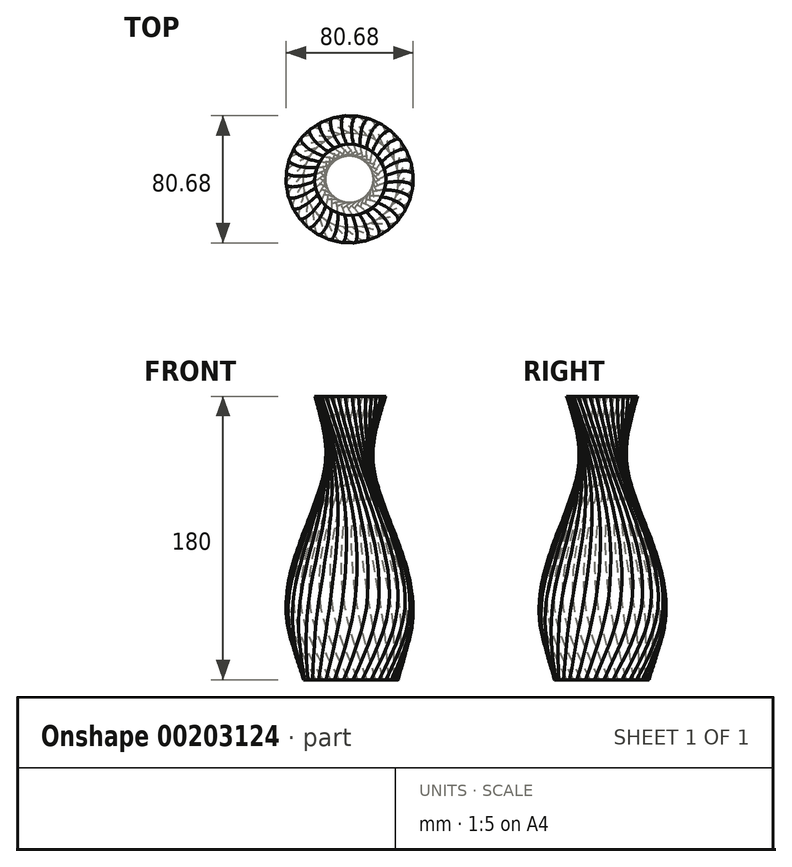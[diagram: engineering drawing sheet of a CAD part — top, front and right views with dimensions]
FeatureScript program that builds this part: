
annotation { "Feature Type Name" : "Feature", "Feature Type Description" : "" }
export const myFeature = defineFeature(function(context is Context, id is Id, definition is map)
    precondition{}
    {
        {
            var Q0;
            Q0=qCreatedBy(makeId("Top.planeOp"),FACE);
            var sketch = newSketch(context, id + "F0", { "sketchPlane" : qUnion([Q0])});
            skCircle(sketch, "E0.cCircle", {"center": v(0, 0) * mm, "radius": 30 * mm, "construction": true});
            skLineSegment(sketch, "E0.0", {"start": v(25.76, -15.66) * mm, "end": v(22.2, -20.39) * mm});
            skLineSegment(sketch, "E0.1", {"start": v(22.2, -20.39) * mm, "end": v(17.8, -24.33) * mm});
            skLineSegment(sketch, "E0.2", {"start": v(17.8, -24.33) * mm, "end": v(12.71, -27.33) * mm});
            skLineSegment(sketch, "E0.3", {"start": v(12.71, -27.33) * mm, "end": v(7.14, -29.29) * mm});
            skLineSegment(sketch, "E0.4", {"start": v(7.14, -29.29) * mm, "end": v(1.29, -30.12) * mm});
            skLineSegment(sketch, "E0.5", {"start": v(1.29, -30.12) * mm, "end": v(-4.61, -29.79) * mm});
            skLineSegment(sketch, "E0.6", {"start": v(-4.61, -29.79) * mm, "end": v(-10.34, -28.32) * mm});
            skLineSegment(sketch, "E0.7", {"start": v(-10.34, -28.32) * mm, "end": v(-15.66, -25.76) * mm});
            skLineSegment(sketch, "E0.8", {"start": v(-15.66, -25.76) * mm, "end": v(-20.39, -22.2) * mm});
            skLineSegment(sketch, "E0.9", {"start": v(-20.39, -22.2) * mm, "end": v(-24.33, -17.8) * mm});
            skLineSegment(sketch, "E0.10", {"start": v(-24.33, -17.8) * mm, "end": v(-27.33, -12.71) * mm});
            skLineSegment(sketch, "E0.11", {"start": v(-27.33, -12.71) * mm, "end": v(-29.29, -7.14) * mm});
            skLineSegment(sketch, "E0.12", {"start": v(-29.29, -7.14) * mm, "end": v(-30.12, -1.29) * mm});
            skLineSegment(sketch, "E0.13", {"start": v(-30.12, -1.29) * mm, "end": v(-29.79, 4.61) * mm});
            skLineSegment(sketch, "E0.14", {"start": v(-29.79, 4.61) * mm, "end": v(-28.32, 10.34) * mm});
            skLineSegment(sketch, "E0.15", {"start": v(-28.32, 10.34) * mm, "end": v(-25.76, 15.66) * mm});
            skLineSegment(sketch, "E0.16", {"start": v(-25.76, 15.66) * mm, "end": v(-22.2, 20.39) * mm});
            skLineSegment(sketch, "E0.17", {"start": v(-22.2, 20.39) * mm, "end": v(-17.8, 24.33) * mm});
            skLineSegment(sketch, "E0.18", {"start": v(-17.8, 24.33) * mm, "end": v(-12.71, 27.33) * mm});
            skLineSegment(sketch, "E0.19", {"start": v(-12.71, 27.33) * mm, "end": v(-7.14, 29.29) * mm});
            skLineSegment(sketch, "E0.20", {"start": v(-7.14, 29.29) * mm, "end": v(-1.29, 30.12) * mm});
            skLineSegment(sketch, "E0.21", {"start": v(-1.29, 30.12) * mm, "end": v(4.61, 29.79) * mm});
            skLineSegment(sketch, "E0.22", {"start": v(4.61, 29.79) * mm, "end": v(10.34, 28.32) * mm});
            skLineSegment(sketch, "E0.23", {"start": v(10.34, 28.32) * mm, "end": v(15.66, 25.76) * mm});
            skLineSegment(sketch, "E0.24", {"start": v(15.66, 25.76) * mm, "end": v(20.39, 22.2) * mm});
            skLineSegment(sketch, "E0.25", {"start": v(20.39, 22.2) * mm, "end": v(24.33, 17.8) * mm});
            skLineSegment(sketch, "E0.26", {"start": v(24.33, 17.8) * mm, "end": v(27.33, 12.71) * mm});
            skLineSegment(sketch, "E0.27", {"start": v(27.33, 12.71) * mm, "end": v(29.29, 7.14) * mm});
            skLineSegment(sketch, "E0.28", {"start": v(29.29, 7.14) * mm, "end": v(30.12, 1.29) * mm});
            skLineSegment(sketch, "E0.29", {"start": v(30.12, 1.29) * mm, "end": v(29.79, -4.61) * mm});
            skLineSegment(sketch, "E0.30", {"start": v(29.79, -4.61) * mm, "end": v(28.32, -10.34) * mm});
            skLineSegment(sketch, "E0.31", {"start": v(28.32, -10.34) * mm, "end": v(25.76, -15.66) * mm});
            skPoint(sketch, "E0.0.midPoint", {"position": v(23.98, -18.02) * mm});
            skSolve(sketch);
        }
        {
            var Q0;
            Q0=qCreatedBy(makeId("Top.planeOp"),FACE);
            cPlane(context, id + "F1", {"entities" : qUnion([Q0]), "cplaneType" : CPlaneType.OFFSET, "offset" : 40 * mm, "width" : 150 * mm, "height" : 150 * mm});
        }
        {
            var Q0;
            Q0=qCreatedBy(id+"F1.planeOp",FACE);
            var sketch = newSketch(context, id + "F2", { "sketchPlane" : qUnion([Q0])});
            skCircle(sketch, "E1.cCircle", {"center": v(-0.7, 0.53) * mm, "radius": 40 * mm, "construction": true});
            skLineSegment(sketch, "E1.0", {"start": v(33.64, -20.35) * mm, "end": v(28.9, -26.65) * mm});
            skLineSegment(sketch, "E1.1", {"start": v(28.9, -26.65) * mm, "end": v(23.03, -31.9) * mm});
            skLineSegment(sketch, "E1.2", {"start": v(23.03, -31.9) * mm, "end": v(16.25, -35.91) * mm});
            skLineSegment(sketch, "E1.3", {"start": v(16.25, -35.91) * mm, "end": v(8.81, -38.52) * mm});
            skLineSegment(sketch, "E1.4", {"start": v(8.81, -38.52) * mm, "end": v(1, -39.63) * mm});
            skLineSegment(sketch, "E1.5", {"start": v(1, -39.63) * mm, "end": v(-6.86, -39.19) * mm});
            skLineSegment(sketch, "E1.6", {"start": v(-6.86, -39.19) * mm, "end": v(-14.49, -37.23) * mm});
            skLineSegment(sketch, "E1.7", {"start": v(-14.49, -37.23) * mm, "end": v(-21.59, -33.81) * mm});
            skLineSegment(sketch, "E1.8", {"start": v(-21.59, -33.81) * mm, "end": v(-27.89, -29.08) * mm});
            skLineSegment(sketch, "E1.9", {"start": v(-27.89, -29.08) * mm, "end": v(-33.14, -23.2) * mm});
            skLineSegment(sketch, "E1.10", {"start": v(-33.14, -23.2) * mm, "end": v(-37.15, -16.42) * mm});
            skLineSegment(sketch, "E1.11", {"start": v(-37.15, -16.42) * mm, "end": v(-39.76, -8.99) * mm});
            skLineSegment(sketch, "E1.12", {"start": v(-39.76, -8.99) * mm, "end": v(-40.86, -1.18) * mm});
            skLineSegment(sketch, "E1.13", {"start": v(-40.86, -1.18) * mm, "end": v(-40.43, 6.68) * mm});
            skLineSegment(sketch, "E1.14", {"start": v(-40.43, 6.68) * mm, "end": v(-38.46, 14.31) * mm});
            skLineSegment(sketch, "E1.15", {"start": v(-38.46, 14.31) * mm, "end": v(-35.05, 21.41) * mm});
            skLineSegment(sketch, "E1.16", {"start": v(-35.05, 21.41) * mm, "end": v(-30.31, 27.71) * mm});
            skLineSegment(sketch, "E1.17", {"start": v(-30.31, 27.71) * mm, "end": v(-24.44, 32.97) * mm});
            skLineSegment(sketch, "E1.18", {"start": v(-24.44, 32.97) * mm, "end": v(-17.66, 36.97) * mm});
            skLineSegment(sketch, "E1.19", {"start": v(-17.66, 36.97) * mm, "end": v(-10.22, 39.58) * mm});
            skLineSegment(sketch, "E1.20", {"start": v(-10.22, 39.58) * mm, "end": v(-2.42, 40.69) * mm});
            skLineSegment(sketch, "E1.21", {"start": v(-2.42, 40.69) * mm, "end": v(5.45, 40.25) * mm});
            skLineSegment(sketch, "E1.22", {"start": v(5.45, 40.25) * mm, "end": v(13.08, 38.29) * mm});
            skLineSegment(sketch, "E1.23", {"start": v(13.08, 38.29) * mm, "end": v(20.18, 34.87) * mm});
            skLineSegment(sketch, "E1.24", {"start": v(20.18, 34.87) * mm, "end": v(26.48, 30.14) * mm});
            skLineSegment(sketch, "E1.25", {"start": v(26.48, 30.14) * mm, "end": v(31.73, 24.27) * mm});
            skLineSegment(sketch, "E1.26", {"start": v(31.73, 24.27) * mm, "end": v(35.74, 17.48) * mm});
            skLineSegment(sketch, "E1.27", {"start": v(35.74, 17.48) * mm, "end": v(38.35, 10.05) * mm});
            skLineSegment(sketch, "E1.28", {"start": v(38.35, 10.05) * mm, "end": v(39.45, 2.25) * mm});
            skLineSegment(sketch, "E1.29", {"start": v(39.45, 2.25) * mm, "end": v(39.01, -5.62) * mm});
            skLineSegment(sketch, "E1.30", {"start": v(39.01, -5.62) * mm, "end": v(37.05, -13.25) * mm});
            skLineSegment(sketch, "E1.31", {"start": v(37.05, -13.25) * mm, "end": v(33.64, -20.35) * mm});
            skPoint(sketch, "E1.0.midPoint", {"position": v(31.27, -23.5) * mm});
            skSolve(sketch);
        }
        {
            var Q0;
            Q0=qCreatedBy(id+"F1.planeOp",FACE);
            cPlane(context, id + "F3", {"entities" : qUnion([Q0]), "cplaneType" : CPlaneType.OFFSET, "offset" : 100 * mm, "width" : 150 * mm, "height" : 150 * mm});
        }
        {
            var Q0;
            Q0=qCreatedBy(id+"F3.planeOp",FACE);
            var sketch = newSketch(context, id + "F4", { "sketchPlane" : qUnion([Q0])});
            skCircle(sketch, "E2.cCircle", {"center": v(-0.94, 0.7) * mm, "radius": 15 * mm, "construction": true});
            skLineSegment(sketch, "E2.0", {"start": v(11.94, -7.12) * mm, "end": v(10.16, -9.49) * mm});
            skLineSegment(sketch, "E2.1", {"start": v(10.16, -9.49) * mm, "end": v(7.96, -11.46) * mm});
            skLineSegment(sketch, "E2.2", {"start": v(7.96, -11.46) * mm, "end": v(5.42, -12.96) * mm});
            skLineSegment(sketch, "E2.3", {"start": v(5.42, -12.96) * mm, "end": v(2.63, -13.94) * mm});
            skLineSegment(sketch, "E2.4", {"start": v(2.63, -13.94) * mm, "end": v(-0.3, -14.35) * mm});
            skLineSegment(sketch, "E2.5", {"start": v(-0.3, -14.35) * mm, "end": v(-3.25, -14.19) * mm});
            skLineSegment(sketch, "E2.6", {"start": v(-3.25, -14.19) * mm, "end": v(-6.1, -13.45) * mm});
            skLineSegment(sketch, "E2.7", {"start": v(-6.1, -13.45) * mm, "end": v(-8.77, -12.17) * mm});
            skLineSegment(sketch, "E2.8", {"start": v(-8.77, -12.17) * mm, "end": v(-11.13, -10.4) * mm});
            skLineSegment(sketch, "E2.9", {"start": v(-11.13, -10.4) * mm, "end": v(-13.1, -8.2) * mm});
            skLineSegment(sketch, "E2.10", {"start": v(-13.1, -8.2) * mm, "end": v(-14.6, -5.65) * mm});
            skLineSegment(sketch, "E2.11", {"start": v(-14.6, -5.65) * mm, "end": v(-15.58, -2.86) * mm});
            skLineSegment(sketch, "E2.12", {"start": v(-15.58, -2.86) * mm, "end": v(-16, 0.06) * mm});
            skLineSegment(sketch, "E2.13", {"start": v(-16, 0.06) * mm, "end": v(-15.84, 3.01) * mm});
            skLineSegment(sketch, "E2.14", {"start": v(-15.84, 3.01) * mm, "end": v(-15.1, 5.88) * mm});
            skLineSegment(sketch, "E2.15", {"start": v(-15.1, 5.88) * mm, "end": v(-13.82, 8.54) * mm});
            skLineSegment(sketch, "E2.16", {"start": v(-13.82, 8.54) * mm, "end": v(-12.04, 10.9) * mm});
            skLineSegment(sketch, "E2.17", {"start": v(-12.04, 10.9) * mm, "end": v(-9.84, 12.87) * mm});
            skLineSegment(sketch, "E2.18", {"start": v(-9.84, 12.87) * mm, "end": v(-7.3, 14.37) * mm});
            skLineSegment(sketch, "E2.19", {"start": v(-7.3, 14.37) * mm, "end": v(-4.5, 15.35) * mm});
            skLineSegment(sketch, "E2.20", {"start": v(-4.5, 15.35) * mm, "end": v(-1.58, 15.77) * mm});
            skLineSegment(sketch, "E2.21", {"start": v(-1.58, 15.77) * mm, "end": v(1.37, 15.6) * mm});
            skLineSegment(sketch, "E2.22", {"start": v(1.37, 15.6) * mm, "end": v(4.23, 14.87) * mm});
            skLineSegment(sketch, "E2.23", {"start": v(4.23, 14.87) * mm, "end": v(6.9, 13.59) * mm});
            skLineSegment(sketch, "E2.24", {"start": v(6.9, 13.59) * mm, "end": v(9.25, 11.8) * mm});
            skLineSegment(sketch, "E2.25", {"start": v(9.25, 11.8) * mm, "end": v(11.22, 9.6) * mm});
            skLineSegment(sketch, "E2.26", {"start": v(11.22, 9.6) * mm, "end": v(12.73, 7.06) * mm});
            skLineSegment(sketch, "E2.27", {"start": v(12.73, 7.06) * mm, "end": v(13.7, 4.28) * mm});
            skLineSegment(sketch, "E2.28", {"start": v(13.7, 4.28) * mm, "end": v(14.12, 1.35) * mm});
            skLineSegment(sketch, "E2.29", {"start": v(14.12, 1.35) * mm, "end": v(13.95, -1.6) * mm});
            skLineSegment(sketch, "E2.30", {"start": v(13.95, -1.6) * mm, "end": v(13.22, -4.46) * mm});
            skLineSegment(sketch, "E2.31", {"start": v(13.22, -4.46) * mm, "end": v(11.94, -7.12) * mm});
            skPoint(sketch, "E2.0.midPoint", {"position": v(11.05, -8.3) * mm});
            skSolve(sketch);
        }
        {
            var Q0;
            Q0=qCreatedBy(id+"F3.planeOp",FACE);
            cPlane(context, id + "F5", {"entities" : qUnion([Q0]), "cplaneType" : CPlaneType.OFFSET, "offset" : 40 * mm, "width" : 150 * mm, "height" : 150 * mm});
        }
        {
            var Q0;
            Q0=qCreatedBy(id+"F5.planeOp",FACE);
            var sketch = newSketch(context, id + "F6", { "sketchPlane" : qUnion([Q0])});
            skCircle(sketch, "E3.cCircle", {"center": v(-0.35, 0.27) * mm, "radius": 22.5 * mm, "construction": true});
            skLineSegment(sketch, "E3.0", {"start": v(18.96, -11.48) * mm, "end": v(16.3, -15.03) * mm});
            skLineSegment(sketch, "E3.1", {"start": v(16.3, -15.03) * mm, "end": v(13, -17.98) * mm});
            skLineSegment(sketch, "E3.2", {"start": v(13, -17.98) * mm, "end": v(9.18, -20.23) * mm});
            skLineSegment(sketch, "E3.3", {"start": v(9.18, -20.23) * mm, "end": v(5, -21.7) * mm});
            skLineSegment(sketch, "E3.4", {"start": v(5, -21.7) * mm, "end": v(0.61, -22.32) * mm});
            skLineSegment(sketch, "E3.5", {"start": v(0.61, -22.32) * mm, "end": v(-3.81, -22.08) * mm});
            skLineSegment(sketch, "E3.6", {"start": v(-3.81, -22.08) * mm, "end": v(-8.1, -20.97) * mm});
            skLineSegment(sketch, "E3.7", {"start": v(-8.1, -20.97) * mm, "end": v(-12.1, -19.05) * mm});
            skLineSegment(sketch, "E3.8", {"start": v(-12.1, -19.05) * mm, "end": v(-15.64, -16.39) * mm});
            skLineSegment(sketch, "E3.9", {"start": v(-15.64, -16.39) * mm, "end": v(-18.6, -13.09) * mm});
            skLineSegment(sketch, "E3.10", {"start": v(-18.6, -13.09) * mm, "end": v(-20.85, -9.27) * mm});
            skLineSegment(sketch, "E3.11", {"start": v(-20.85, -9.27) * mm, "end": v(-22.32, -5.09) * mm});
            skLineSegment(sketch, "E3.12", {"start": v(-22.32, -5.09) * mm, "end": v(-22.94, -0.7) * mm});
            skLineSegment(sketch, "E3.13", {"start": v(-22.94, -0.7) * mm, "end": v(-22.7, 3.73) * mm});
            skLineSegment(sketch, "E3.14", {"start": v(-22.7, 3.73) * mm, "end": v(-21.6, 8.02) * mm});
            skLineSegment(sketch, "E3.15", {"start": v(-21.6, 8.02) * mm, "end": v(-19.67, 12.01) * mm});
            skLineSegment(sketch, "E3.16", {"start": v(-19.67, 12.01) * mm, "end": v(-17, 15.56) * mm});
            skLineSegment(sketch, "E3.17", {"start": v(-17, 15.56) * mm, "end": v(-13.7, 18.51) * mm});
            skLineSegment(sketch, "E3.18", {"start": v(-13.7, 18.51) * mm, "end": v(-9.89, 20.76) * mm});
            skLineSegment(sketch, "E3.19", {"start": v(-9.89, 20.76) * mm, "end": v(-5.7, 22.23) * mm});
            skLineSegment(sketch, "E3.20", {"start": v(-5.7, 22.23) * mm, "end": v(-1.32, 22.85) * mm});
            skLineSegment(sketch, "E3.21", {"start": v(-1.32, 22.85) * mm, "end": v(3.1, 22.6) * mm});
            skLineSegment(sketch, "E3.22", {"start": v(3.1, 22.6) * mm, "end": v(7.4, 21.5) * mm});
            skLineSegment(sketch, "E3.23", {"start": v(7.4, 21.5) * mm, "end": v(11.4, 19.58) * mm});
            skLineSegment(sketch, "E3.24", {"start": v(11.4, 19.58) * mm, "end": v(14.94, 16.92) * mm});
            skLineSegment(sketch, "E3.25", {"start": v(14.94, 16.92) * mm, "end": v(17.9, 13.62) * mm});
            skLineSegment(sketch, "E3.26", {"start": v(17.9, 13.62) * mm, "end": v(20.15, 9.8) * mm});
            skLineSegment(sketch, "E3.27", {"start": v(20.15, 9.8) * mm, "end": v(21.61, 5.62) * mm});
            skLineSegment(sketch, "E3.28", {"start": v(21.61, 5.62) * mm, "end": v(22.24, 1.23) * mm});
            skLineSegment(sketch, "E3.29", {"start": v(22.24, 1.23) * mm, "end": v(21.99, -3.2) * mm});
            skLineSegment(sketch, "E3.30", {"start": v(21.99, -3.2) * mm, "end": v(20.89, -7.49) * mm});
            skLineSegment(sketch, "E3.31", {"start": v(20.89, -7.49) * mm, "end": v(18.96, -11.48) * mm});
            skPoint(sketch, "E3.0.midPoint", {"position": v(17.63, -13.25) * mm});
            skSolve(sketch);
        }
        {
            var Q0;
            Q0 = qSketchRegion(id + "F0", true);
            var Q1;
            Q1 = qSketchRegion(id + "F2", true);
            var Q2;
            Q2 = qSketchRegion(id + "F4", true);
            var Q3;
            Q3 = qSketchRegion(id + "F6", true);
            var Q4;
            Q4=sQuery(id+"F0.wireOp",VERTEX,"E0.31.end");
            var Q5;
            Q5=sQuery(id+"F2.wireOp",VERTEX,"E1.30.start");
            var Q6;
            Q6=sQuery(id+"F4.wireOp",VERTEX,"E2.0.start");
            var Q7;
            Q7=sQuery(id+"F6.wireOp",VERTEX,"E3.3.start");
            loft(context, id + "F7", {"sheetProfilesArray" : [{ "sheetProfileEntities" : qUnion([Q0]) }, { "sheetProfileEntities" : qUnion([Q1]) }, { "sheetProfileEntities" : qUnion([Q2]) }, { "sheetProfileEntities" : qUnion([Q3]) }], "matchConnections" : true, "connections" : [{ "connectionEntities" : qUnion([Q4, Q5, Q6, Q7]), "connectionEdgeQueries" : qUnion([]), "connectionEdgeParameters" : [] }]});
        }
    });
